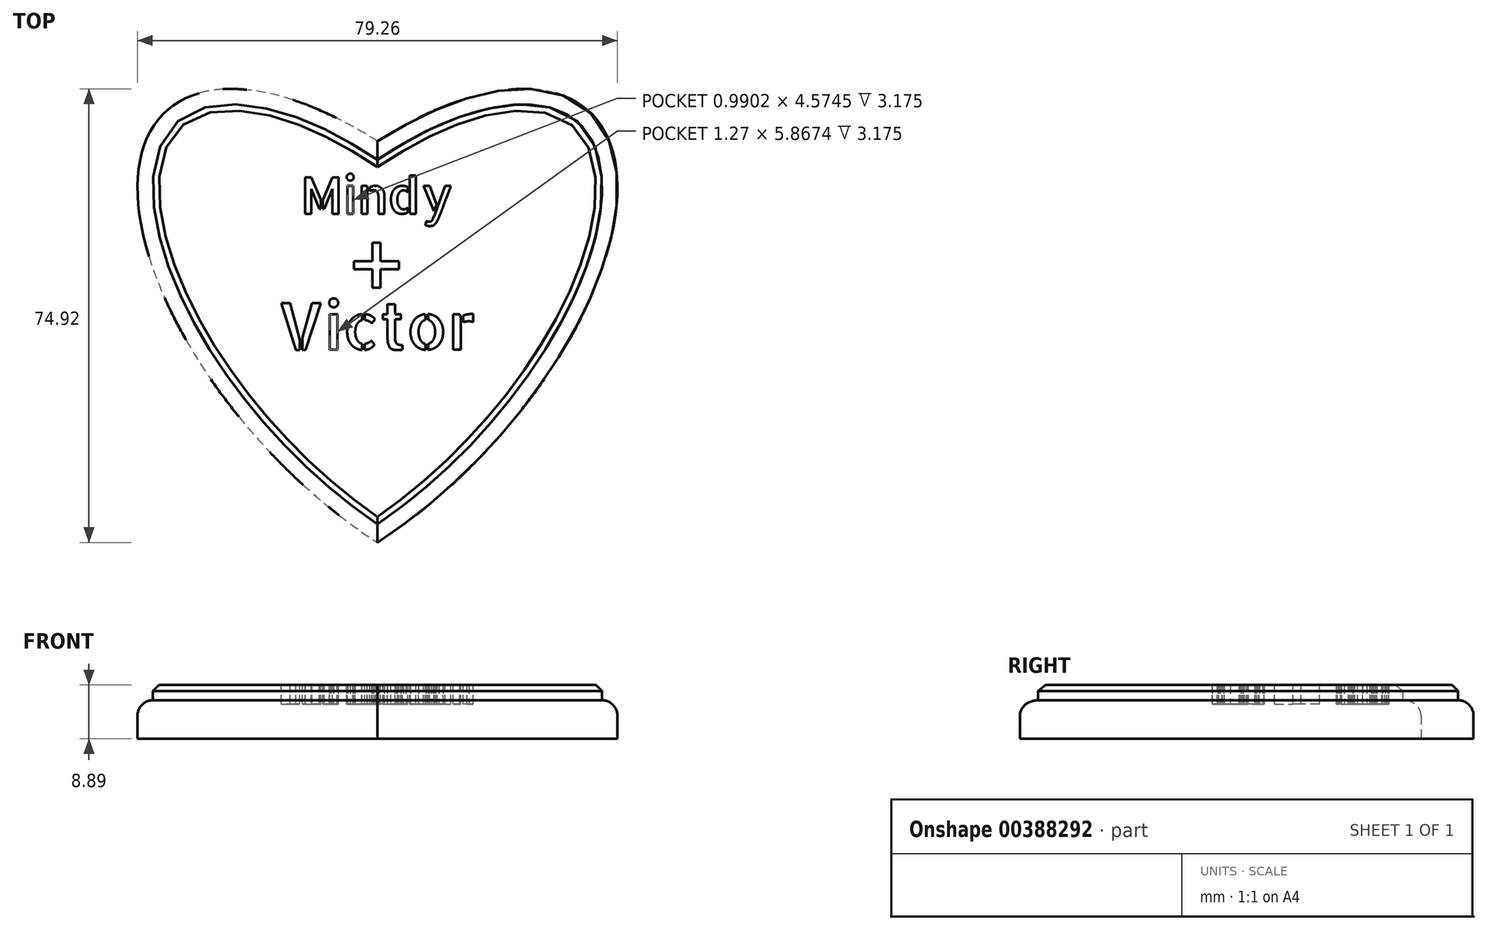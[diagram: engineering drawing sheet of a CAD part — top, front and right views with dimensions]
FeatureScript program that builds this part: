
annotation { "Feature Type Name" : "Feature", "Feature Type Description" : "" }
export const myFeature = defineFeature(function(context is Context, id is Id, definition is map)
    precondition{}
    {
        {
            var Q0;
            Q0=qCreatedBy(makeId("Top.planeOp"),FACE);
            var sketch = newSketch(context, id + "F0", { "sketchPlane" : qUnion([Q0])});
            skLineSegment(sketch, "E0.bottom", {"start": v(-34.92, 38.1) * mm, "end": v(34.93, 38.1) * mm});
            skLineSegment(sketch, "E0.top", {"start": v(-34.93, -38.1) * mm, "end": v(34.92, -38.1) * mm});
            skLineSegment(sketch, "E0.left", {"start": v(-34.92, 38.1) * mm, "end": v(-34.93, -38.1) * mm});
            skLineSegment(sketch, "E0.right", {"start": v(34.93, 38.1) * mm, "end": v(34.92, -38.1) * mm});
            skPoint(sketch, "E0.middle", {"position": v(0, 0) * mm});
            skEllipse(sketch, "E1", {"center": v(0, 0) * mm, "majorRadius": 51.69 * mm, "minorRadius": 25.4 * mm, "majorAxis": v(-0.68, 0.74)});
            skEllipse(sketch, "E2", {"center": v(0, 0) * mm, "majorRadius": 51.69 * mm, "minorRadius": 25.4 * mm, "majorAxis": v(0.68, 0.74)});
            skSolve(sketch);
        }
        {
            var Q0;
            {var subQ0=sQuery(id+"F0.wireOp",EDGE,"E2");var subQ1=sQuery(id+"F0.wireOp",EDGE,"E1");var subQ2=makeQuery(id+"F0.imprint","INTERSECT",VERTEX,{"disambiguationData":[OD(0.0)],"derivedFrom":[subQ1,subQ0]});Q0=makeQuery(id+"F0.imprint","IMPRINT",FACE,{"disambiguationData":[TD([[makeQuery(id+"F0.imprint","IMPRINT",EDGE,{"disambiguationData":[TD([[subQ2,-1.0]])],"derivedFrom":subQ1}),1.0]])]});}
            var Q1;
            {var subQ0=sQuery(id+"F0.wireOp",EDGE,"E2");var subQ3=sQuery(id+"F0.wireOp",EDGE,"E1");var subQ5=makeQuery(id+"F0.imprint","INTERSECT",VERTEX,{"disambiguationData":[OD(2.0)],"derivedFrom":[subQ3,subQ0]});Q1=makeQuery(id+"F0.imprint","IMPRINT",FACE,{"disambiguationData":[TD([[makeQuery(id+"F0.imprint","IMPRINT",EDGE,{"disambiguationData":[TD([[subQ5,-1.0]])],"derivedFrom":subQ3}),-1.0]])]});}
            var Q2;
            {var subQ0=sQuery(id+"F0.wireOp",EDGE,"E1");var subQ1=sQuery(id+"F0.wireOp",EDGE,"E0.left");var subQ2=makeQuery(id+"F0.imprint","INTERSECT",VERTEX,{"derivedFrom":[subQ1,subQ0]});Q2=makeQuery(id+"F0.imprint","IMPRINT",FACE,{"disambiguationData":[TD([[makeQuery(id+"F0.imprint","IMPRINT",EDGE,{"disambiguationData":[TD([[subQ2,-1.0]])],"derivedFrom":subQ0}),1.0]])]});}
            var Q3;
            {var subQ0=sQuery(id+"F0.wireOp",EDGE,"E1");var subQ1=sQuery(id+"F0.wireOp",EDGE,"E0.left");var subQ3=makeQuery(id+"F0.imprint","INTERSECT",VERTEX,{"derivedFrom":[subQ1,subQ0]});Q3=makeQuery(id+"F0.imprint","IMPRINT",FACE,{"disambiguationData":[TD([[makeQuery(id+"F0.imprint","IMPRINT",EDGE,{"disambiguationData":[TD([[subQ3,1.0]])],"derivedFrom":subQ1}),-1.0]])]});}
            var Q4;
            {var subQ0=sQuery(id+"F0.wireOp",EDGE,"E2");var subQ1=sQuery(id+"F0.wireOp",EDGE,"E0.right");var subQ3=makeQuery(id+"F0.imprint","INTERSECT",VERTEX,{"derivedFrom":[subQ1,subQ0]});Q4=makeQuery(id+"F0.imprint","IMPRINT",FACE,{"disambiguationData":[TD([[makeQuery(id+"F0.imprint","IMPRINT",EDGE,{"disambiguationData":[TD([[subQ3,1.0]])],"derivedFrom":subQ1}),1.0]])]});}
            var Q5;
            {var subQ0=sQuery(id+"F0.wireOp",EDGE,"E1");var subQ1=sQuery(id+"F0.wireOp",EDGE,"E0.bottom");var subQ3=makeQuery(id+"F0.imprint","INTERSECT",VERTEX,{"derivedFrom":[subQ1,subQ0]});Q5=makeQuery(id+"F0.imprint","IMPRINT",FACE,{"disambiguationData":[TD([[makeQuery(id+"F0.imprint","IMPRINT",EDGE,{"disambiguationData":[TD([[subQ3,1.0]])],"derivedFrom":subQ1}),1.0]])]});}
            var Q6;
            {var subQ0=sQuery(id+"F0.wireOp",EDGE,"E2");var subQ1=sQuery(id+"F0.wireOp",EDGE,"E0.bottom");var subQ3=makeQuery(id+"F0.imprint","INTERSECT",VERTEX,{"derivedFrom":[subQ1,subQ0]});Q6=makeQuery(id+"F0.imprint","IMPRINT",FACE,{"disambiguationData":[TD([[makeQuery(id+"F0.imprint","IMPRINT",EDGE,{"disambiguationData":[TD([[subQ3,-1.0]])],"derivedFrom":subQ1}),1.0]])]});}
            extrude(context, id + "F1", {"entities" : qUnion([Q0, Q1, Q2, Q3, Q4, Q5, Q6]), "depth" : 6.35 * mm});
        }
        {
            var Q0;
            Q0=makeQuery(id+"F1.opExtrude","CAP_EDGE",EDGE,{"disambiguationData":[OSD([sQuery(id+"F0.wireOp",EDGE,"E1")])],"isStart":false});
            var Q1;
            Q1=makeQuery(id+"F1.opExtrude","CAP_EDGE",EDGE,{"disambiguationData":[OSD([sQuery(id+"F0.wireOp",EDGE,"E2")])],"isStart":false});
            fillet(context, id + "F2", {"entities" : qUnion([Q0, Q1]), "radius" : 2.54 * mm, "tangentPropagation" : true, "allowEdgeOverflow" : false});
        }
        {
            var Q0;
            Q0=makeQuery(id+"F1.opExtrude","CAP_FACE",FACE,{"disambiguationData":[OSD([sQuery(id+"F0.wireOp",EDGE,"E1"),sQuery(id+"F0.wireOp",EDGE,"E2")])],"isStart":false});
            extrude(context, id + "F3", {"entities" : qUnion([Q0]), "operationType" : NewBodyOperationType.ADD, "depth" : 2.54 * mm});
        }
        {
            var Q0;
            {var subQ0=sQuery(id+"F0.wireOp",EDGE,"E2");var subQ1=sQuery(id+"F0.wireOp",EDGE,"E1");Q0=makeQuery(id+"F3.opExtrude","CAP_EDGE",EDGE,{"disambiguationData":[OSD([subQ1,subQ0]),TDD([makeQuery(id+"F2.opFillet","BLEND_EDGE",EDGE,{"blendedFrom":[makeQuery(id+"F1.opExtrude","CAP_EDGE",EDGE,{"disambiguationData":[OSD([subQ1])],"isStart":false}),makeQuery(id+"F1.opExtrude","CAP_FACE",FACE,{"disambiguationData":[OSD([subQ1,subQ0])],"isStart":false})],"blendedInto":[makeQuery(id+"F1.opExtrude","CAP_FACE",FACE,{"disambiguationData":[OSD([subQ1,subQ0])],"isStart":false})]})])],"isStart":false});}
            var Q1;
            {var subQ0=sQuery(id+"F0.wireOp",EDGE,"E2");var subQ1=sQuery(id+"F0.wireOp",EDGE,"E1");Q1=makeQuery(id+"F3.opExtrude","CAP_EDGE",EDGE,{"disambiguationData":[OSD([subQ1,subQ0]),TDD([makeQuery(id+"F2.opFillet","BLEND_EDGE",EDGE,{"blendedFrom":[makeQuery(id+"F1.opExtrude","CAP_EDGE",EDGE,{"disambiguationData":[OSD([subQ0])],"isStart":false}),makeQuery(id+"F1.opExtrude","CAP_FACE",FACE,{"disambiguationData":[OSD([subQ1,subQ0])],"isStart":false})],"blendedInto":[makeQuery(id+"F1.opExtrude","CAP_FACE",FACE,{"disambiguationData":[OSD([subQ1,subQ0])],"isStart":false})]})])],"isStart":false});}
            chamfer(context, id + "F4", {"entities" : qUnion([Q0, Q1]), "width" : 1.02 * mm, "tangentPropagation" : true});
        }
        {
            var Q0;
            Q0=makeQuery(id+"F3.opExtrude","CAP_FACE",FACE,{"disambiguationData":[OSD([sQuery(id+"F0.wireOp",EDGE,"E1"),sQuery(id+"F0.wireOp",EDGE,"E2")])],"isStart":false});
            var sketch = newSketch(context, id + "F5", { "sketchPlane" : qUnion([Q0])});
            skText(sketch, "E3", { "text": "Mindy\n", "fontName": "AllertaStencil-Regular.ttf"});
            skText(sketch, "E4", { "text": "+", "fontName": "AllertaStencil-Regular.ttf"});
            skText(sketch, "E5", { "text": "Victor", "fontName": "AllertaStencil-Regular.ttf"});
            const initialGuessF5  = {"E3": [-0.0127, 0.02118, 1, 0, 0.00598], "E4": [-0.00445, 0.00893, 1, 0, 0.00972], "E5": [-0.01649, -0.00128, 1, 0, 0.00767]};
            skSetInitialGuess(sketch, initialGuessF5);
            skSolve(sketch);
        }
        {
            var Q0;
            Q0=qSketchRegion(id+"F5",true);
            extrude(context, id + "F6", {"entities" : qUnion([Q0]), "operationType" : NewBodyOperationType.REMOVE, "oppositeDirection" : true, "depth" : 3.17 * mm});
        }
    });
